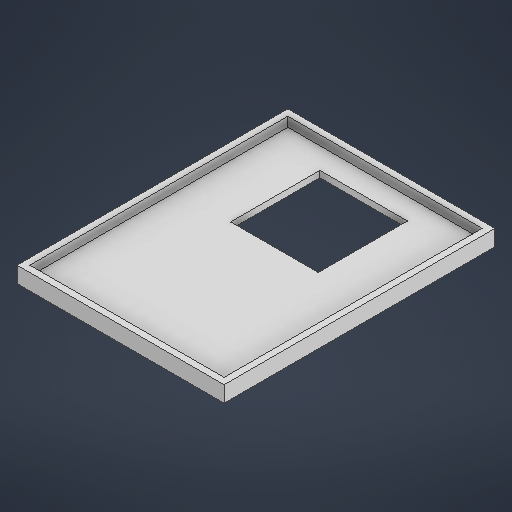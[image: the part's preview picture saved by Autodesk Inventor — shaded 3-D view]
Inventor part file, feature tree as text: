
AUTODESK INVENTOR PART (.ipt)
format: ipt  version: 2025 (Build 290162010, 162A)  size: 211,456 bytes
history: native  units: mm
features: extrude x2, sketch x1
ambient origin geometry x8: Origin, YZ Plane, XZ Plane, XY Plane, X Axis, Y Axis, Z Axis, Center Point
bodies: Solid1 (feature_tree)
feature tree (3):
  sketch  "Sketch1"  dims[d14=2.0mm d15=0.0mm d16=5.0mm d17=0.0mm]
  extrude  "Extrusion1"  Depth=5.0mm TaperAngle=0.0deg
  extrude  "Extrusion2"  [1 undecoded]
note: 1 required parameter value undecoded (feature->parameter linkage not recoverable at this tier; creation-order binding heuristic only, values carry confidence <= 0.55)
